# Revit family: F1100-C-T
name_source: partatom
category: Plumbing Fixtures
units: mm (PartAtom-declared; Revit-internal decimal feet)

## family parameters
Cut with Voids When Loaded = No
Enable Cutting in Views = No
Host = Face
Maintain Annotation Orientation = No
Part Type = Normal
Room Calculation Point = No
Round Connector Dimension = Use Radius
Shared = No

## types (10) — shared parameters
Description = FLOOR DRAIN WITH ROUND STRAINER AND SOLID SECURED COVER
Domestic Cold Water Radius = 0.25 "
Floor Drain Material = Paint - Sherwin Williams Paint - #952C2A - Bellwood Red
Manufacturer = MIFAB
Model = F1100-C-T
URL = WWW.MIFAB.COM
zero-valued in all types: CWFU, Default Elevation, WFU

## per-type parameters (varying)
| type | Body Height | Pipe Diameter | Pipe Radius | Strainer Diameter | Strainer Radius |
| 7" Strainer - 2" Drain | 3.375 " | 2 " | 1 " | 7 " | 3.5 " |
| 7" Strainer - 3" Drain | 3.375 " | 3 " | 1.5 " | 7 " | 3.5 " |
| 7" Strainer - 4" Drain | 3.375 " | 4 " | 2 " | 7 " | 3.5 " |
| 7" Strainer - 5" Drain | 3.375 " | 5 " | 2.5 " | 7 " | 3.5 " |
| 7" Strainer - 6" Drain | 4.75 " | 6 " | 3 " | 7 " | 3.5 " |
| 6" Strainer - 2" Drain | 3.375 " | 2 " | 1 " | 6 " | 3 " |
| 6" Strainer - 3" Drain | 3.375 " | 3 " | 1.5 " | 6 " | 3 " |
| 6" Strainer - 4" Drain | 3.375 " | 4 " | 2 " | 6 " | 3 " |
| 6" Strainer - 5" Drain | 3.375 " | 5 " | 2.5 " | 6 " | 3 " |
| 6" Strainer - 6" Drain | 4.75 " | 6 " | 3 " | 6 " | 3 " |

## geometry (parser evidence)
native form markers: Sweep x1
no freeform markers — native parametric forms only
